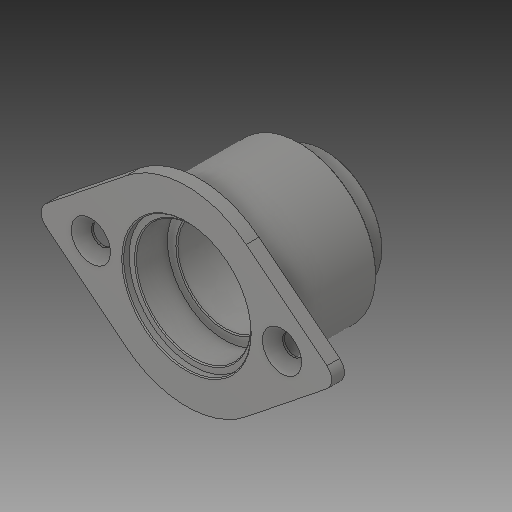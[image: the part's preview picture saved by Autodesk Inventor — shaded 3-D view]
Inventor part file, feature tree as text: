
AUTODESK INVENTOR PART (.ipt)
format: ipt  version: 2019.4 (Build 234330000, 330)  size: 178,688 bytes
history: native  units: in
note: dims shown in document units (in); Inventor stores cm internally (conversion verified against a paired STEP export)
features: chamfer x1
ambient origin geometry x8: Origin, YZ Plane, XZ Plane, XY Plane, X Axis, Y Axis, Z Axis, Center Point
bodies: Solid1 (feature_tree)
feature tree (1):
  chamfer  "Chamfer1"  [1 undecoded]
note: 1 required parameter value undecoded (feature->parameter linkage not recoverable at this tier; creation-order binding heuristic only, values carry confidence <= 0.55)
